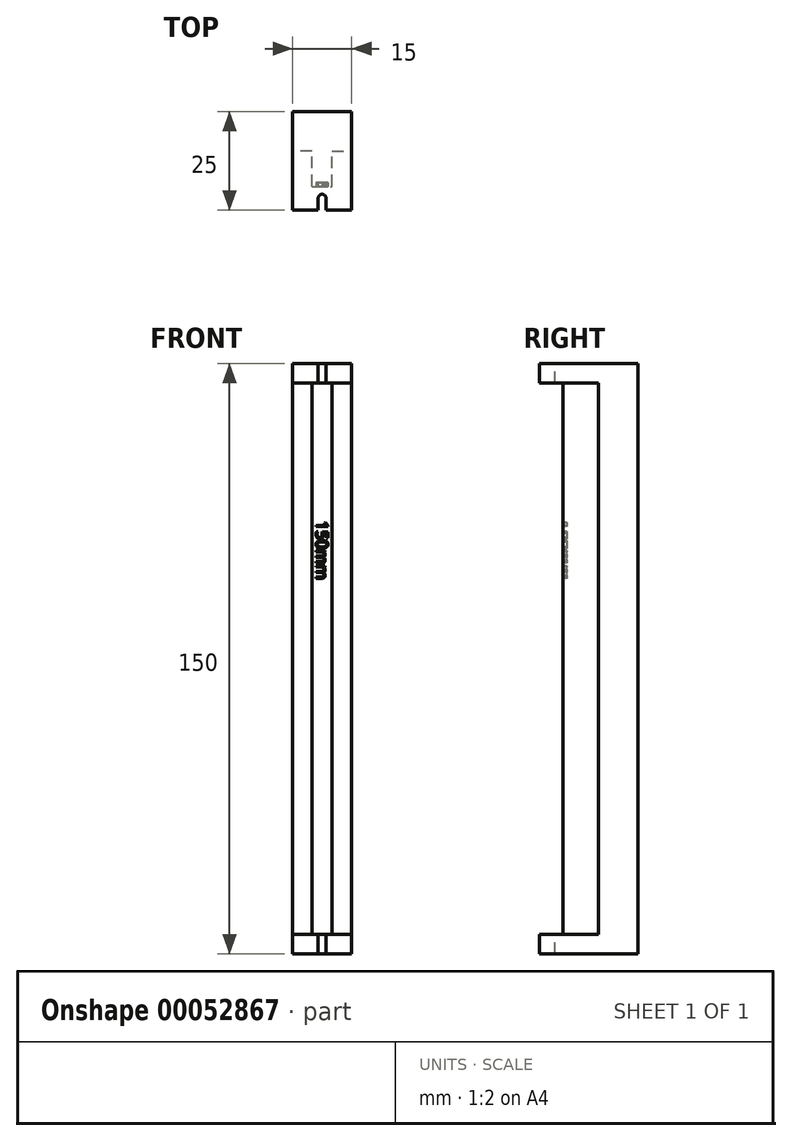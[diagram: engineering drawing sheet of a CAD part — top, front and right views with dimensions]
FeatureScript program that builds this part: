
annotation { "Feature Type Name" : "Feature", "Feature Type Description" : "" }
export const myFeature = defineFeature(function(context is Context, id is Id, definition is map)
    precondition{}
    {
        {
            var Q0;
            Q0=qCreatedBy(makeId("Top.planeOp"),FACE);
            var sketch = newSketch(context, id + "F0", { "sketchPlane" : qUnion([Q0])});
            skLineSegment(sketch, "E0.rect.bottom", {"start": v(7.5, 12.5) * mm, "end": v(-7.5, 12.5) * mm});
            skLineSegment(sketch, "E0.rect.top", {"start": v(7.5, -12.5) * mm, "end": v(-7.5, -12.5) * mm});
            skLineSegment(sketch, "E0.rect.left", {"start": v(7.5, 12.5) * mm, "end": v(7.5, -12.5) * mm});
            skLineSegment(sketch, "E0.rect.right", {"start": v(-7.5, 12.5) * mm, "end": v(-7.5, -12.5) * mm});
            skPoint(sketch, "E0.rect.middle", {"position": v(0, 0) * mm});
            skSolve(sketch);
        }
        {
            var Q0;
            Q0=makeQuery(id+"F0.imprint","IMPRINT",FACE,{"disambiguationData":[TD([[makeQuery(id+"F0.imprint","IMPRINT",EDGE,{"derivedFrom":sQuery(id+"F0.wireOp",EDGE,"E0.rect.bottom")}),1.0]])]});
            extrude(context, id + "F1", {"entities" : qUnion([Q0]), "depth" : 150 * mm});
        }
        {
            var Q0;
            Q0=makeQuery(id+"F1.opExtrude","SWEPT_FACE",FACE,{"disambiguationData":[OSD([sQuery(id+"F0.wireOp",EDGE,"E0.rect.left")])]});
            var sketch = newSketch(context, id + "F2", { "sketchPlane" : qUnion([Q0])});
            skLineSegment(sketch, "E1.bottom", {"start": v(-12.5, 145) * mm, "end": v(2.5, 145) * mm});
            skLineSegment(sketch, "E1.top", {"start": v(-12.5, 5) * mm, "end": v(2.5, 5) * mm});
            skLineSegment(sketch, "E1.left", {"start": v(-12.5, 145) * mm, "end": v(-12.5, 5) * mm});
            skLineSegment(sketch, "E1.right", {"start": v(2.5, 145) * mm, "end": v(2.5, 5) * mm});
            skSolve(sketch);
        }
        {
            var Q0;
            Q0=makeQuery(id+"F2.imprint","IMPRINT",FACE,{"disambiguationData":[TD([[makeQuery(id+"F2.imprint","IMPRINT",EDGE,{"derivedFrom":sQuery(id+"F2.wireOp",EDGE,"E1.bottom")}),-1.0]])]});
            extrude(context, id + "F3", {"entities" : qUnion([Q0]), "operationType" : NewBodyOperationType.REMOVE, "oppositeDirection" : true, "depth" : 5 * mm});
        }
        {
            var Q0;
            Q0=makeQuery(id+"F1.opExtrude","SWEPT_BODY",BODY,{"disambiguationData":[OSD([sQuery(id+"F0.wireOp",EDGE,"E0.rect.bottom"),sQuery(id+"F0.wireOp",EDGE,"E0.rect.top"),sQuery(id+"F0.wireOp",EDGE,"E0.rect.left"),sQuery(id+"F0.wireOp",EDGE,"E0.rect.right")])]});
            var Q1;
            Q1=qCreatedBy(makeId("Right.planeOp"),FACE);
            mirror(context, id + "F4", {"operationType" : NewBodyOperationType.INTERSECT, "entities" : qUnion([Q0]), "mirrorPlane" : qUnion([Q1])});
        }
        {
            var Q0;
            Q0=makeQuery(id+"F1.opExtrude","SWEPT_FACE",FACE,{"disambiguationData":[OSD([sQuery(id+"F0.wireOp",EDGE,"E0.rect.top")])]});
            var sketch = newSketch(context, id + "F5", { "sketchPlane" : qUnion([Q0])});
            skLineSegment(sketch, "E2.bottom", {"start": v(-2.5, 145) * mm, "end": v(2.5, 145) * mm});
            skLineSegment(sketch, "E2.top", {"start": v(-2.5, 5) * mm, "end": v(2.5, 5) * mm});
            skLineSegment(sketch, "E2.left", {"start": v(-2.5, 145) * mm, "end": v(-2.5, 5) * mm});
            skLineSegment(sketch, "E2.right", {"start": v(2.5, 145) * mm, "end": v(2.5, 5) * mm});
            skSolve(sketch);
        }
        {
            var Q0;
            Q0=makeQuery(id+"F5.imprint","IMPRINT",FACE,{"disambiguationData":[TD([[makeQuery(id+"F5.imprint","IMPRINT",EDGE,{"derivedFrom":sQuery(id+"F5.wireOp",EDGE,"E2.bottom")}),-1.0]])]});
            extrude(context, id + "F6", {"entities" : qUnion([Q0]), "operationType" : NewBodyOperationType.REMOVE, "oppositeDirection" : true, "depth" : 6 * mm});
        }
        {
            var Q0;
            Q0=makeQuery(id+"F1.opExtrude","CAP_FACE",FACE,{"disambiguationData":[OSD([sQuery(id+"F0.wireOp",EDGE,"E0.rect.bottom"),sQuery(id+"F0.wireOp",EDGE,"E0.rect.top"),sQuery(id+"F0.wireOp",EDGE,"E0.rect.left"),sQuery(id+"F0.wireOp",EDGE,"E0.rect.right")])],"isStart":false});
            var sketch = newSketch(context, id + "F7", { "sketchPlane" : qUnion([Q0])});
            skLineSegment(sketch, "E3.bottom", {"start": v(-1, -12.5) * mm, "end": v(1, -12.5) * mm});
            skLineSegment(sketch, "E3.left", {"start": v(-1, -12.5) * mm, "end": v(-1, -9.5) * mm});
            skLineSegment(sketch, "E3.right", {"start": v(1, -12.5) * mm, "end": v(1, -9.5) * mm});
            skArc(sketch, "E4", {"start": v(1, -9.5) * mm, "mid": v(0, -8.5) * mm, "end": v(-1, -9.5) * mm});
            skSolve(sketch);
        }
        {
            var Q0;
            Q0=makeQuery(id+"F7.imprint","IMPRINT",FACE,{"disambiguationData":[TD([[makeQuery(id+"F7.imprint","IMPRINT",EDGE,{"derivedFrom":sQuery(id+"F7.wireOp",EDGE,"E3.bottom")}),-1.0]])]});
            extrude(context, id + "F8", {"entities" : qUnion([Q0]), "operationType" : NewBodyOperationType.REMOVE, "endBound" : BoundingType.THROUGH_ALL, "oppositeDirection" : true, "depth" : 25 * mm});
        }
        {
            var Q0;
            Q0=makeQuery(id+"F6.boolean.opBoolean","COPY",FACE,{"derivedFrom":makeQuery(id+"F6.opExtrude","CAP_FACE",FACE,{"disambiguationData":[OSD([sQuery(id+"F5.wireOp",EDGE,"E2.bottom"),sQuery(id+"F5.wireOp",EDGE,"E2.top"),sQuery(id+"F5.wireOp",EDGE,"E2.left"),sQuery(id+"F5.wireOp",EDGE,"E2.right")])],"isStart":false})});
            var sketch = newSketch(context, id + "F9", { "sketchPlane" : qUnion([Q0])});
            skText(sketch, "E5", { "text": "150mm", "fontName": "OpenSans-Regular.ttf"});
            const initialGuessF9  = {"E5": [-0.0015, 0.11, 0, -1, 0.003]};
            skSetInitialGuess(sketch, initialGuessF9);
            skSolve(sketch);
        }
        {
            var Q0;
            Q0=makeQuery(id+"F9.imprint","IMPRINT",FACE,{"disambiguationData":[TD([[makeQuery(id+"F9.imprint","IMPRINT",EDGE,{"derivedFrom":sQuery(id+"F9.wireOp",EDGE,"E5.sketch_text.stroke-0")}),-1.0]])]});
            var Q1;
            Q1=makeQuery(id+"F9.imprint","IMPRINT",FACE,{"disambiguationData":[TD([[makeQuery(id+"F9.imprint","IMPRINT",EDGE,{"derivedFrom":sQuery(id+"F9.wireOp",EDGE,"E5.sketch_text.stroke-9")}),-1.0]])]});
            var Q2;
            Q2=makeQuery(id+"F9.imprint","IMPRINT",FACE,{"disambiguationData":[TD([[makeQuery(id+"F9.imprint","IMPRINT",EDGE,{"derivedFrom":sQuery(id+"F9.wireOp",EDGE,"E5.sketch_text.stroke-28")}),-1.0]])]});
            var Q3;
            Q3=makeQuery(id+"F9.imprint","IMPRINT",FACE,{"disambiguationData":[TD([[makeQuery(id+"F9.imprint","IMPRINT",EDGE,{"derivedFrom":sQuery(id+"F9.wireOp",EDGE,"E5.sketch_text.stroke-44")}),-1.0]])]});
            var Q4;
            Q4=makeQuery(id+"F9.imprint","IMPRINT",FACE,{"disambiguationData":[TD([[makeQuery(id+"F9.imprint","IMPRINT",EDGE,{"derivedFrom":sQuery(id+"F9.wireOp",EDGE,"E5.sketch_text.stroke-72")}),-1.0]])]});
            extrude(context, id + "F10", {"entities" : qUnion([Q0, Q1, Q2, Q3, Q4]), "operationType" : NewBodyOperationType.REMOVE, "oppositeDirection" : true, "depth" : 1 * mm});
        }
    });
